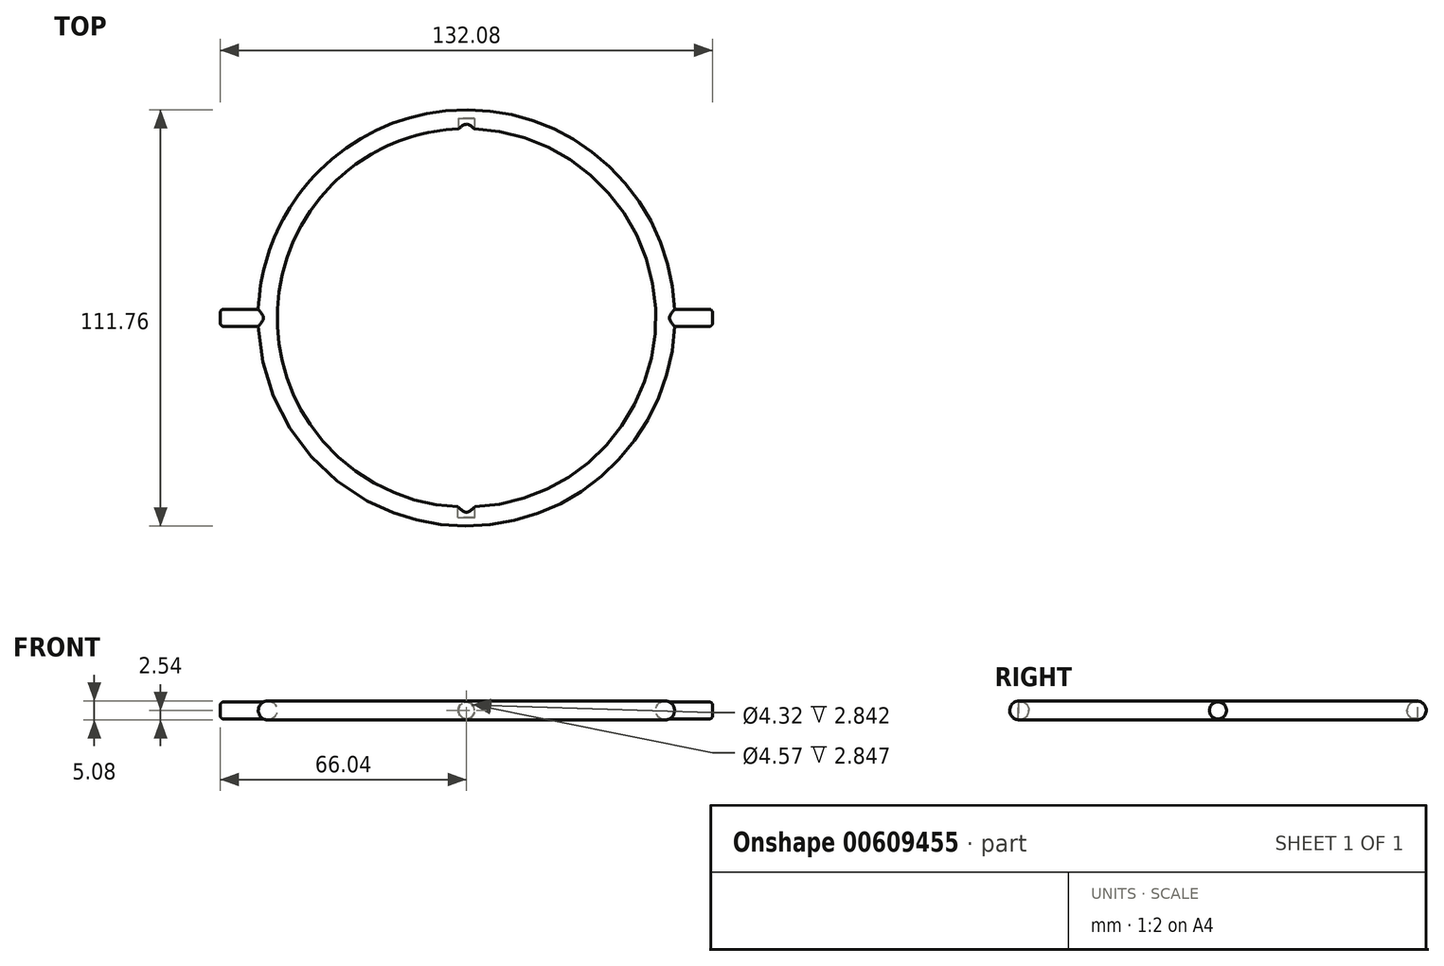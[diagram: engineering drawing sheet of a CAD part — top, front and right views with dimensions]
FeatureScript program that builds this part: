
annotation { "Feature Type Name" : "Feature", "Feature Type Description" : "" }
export const myFeature = defineFeature(function(context is Context, id is Id, definition is map)
    precondition{}
    {
        {
            var Q0;
            Q0=qCreatedBy(makeId("Top.planeOp"),FACE);
            var sketch = newSketch(context, id + "F0", { "sketchPlane" : qUnion([Q0])});
            skCircle(sketch, "E0", {"center": v(0, 0) * mm, "radius": 53.34 * mm});
            skSolve(sketch);
        }
        {
            var Q0;
            Q0=qCreatedBy(makeId("Right.planeOp"),FACE);
            var sketch = newSketch(context, id + "F1", { "sketchPlane" : qUnion([Q0])});
            skCircle(sketch, "E1", {"center": v(-53.34, 0) * mm, "radius": 2.54 * mm});
            skSolve(sketch);
        }
        {
            var Q0;
            Q0=makeQuery(id+"F1.imprint","IMPRINT",FACE,{"disambiguationData":[TD([[makeQuery(id+"F1.imprint","IMPRINT",EDGE,{"derivedFrom":sQuery(id+"F1.wireOp",EDGE,"E1")}),1.0]])]});
            var Q1;
            Q1=sQuery(id+"F0.wireOp",EDGE,"E0");
            sweep(context, id + "F2", {"profiles" : qUnion([Q0]), "path" : qUnion([Q1])});
        }
        {
            var Q0;
            Q0=qCreatedBy(makeId("Front.planeOp"),FACE);
            cPlane(context, id + "F3", {"entities" : qUnion([Q0]), "cplaneType" : CPlaneType.OFFSET, "offset" : 49.53 * mm, "oppositeDirection" : true, "width" : 152.4 * mm, "height" : 152.4 * mm});
        }
        {
            var Q0;
            Q0=qCreatedBy(id+"F3.planeOp",FACE);
            var sketch = newSketch(context, id + "F4", { "sketchPlane" : qUnion([Q0])});
            skCircle(sketch, "E2", {"center": v(0, 0) * mm, "radius": 2.16 * mm});
            skSolve(sketch);
        }
        {
            var Q0;
            Q0=makeQuery(id+"F4.imprint","IMPRINT",FACE,{"disambiguationData":[TD([[makeQuery(id+"F4.imprint","IMPRINT",EDGE,{"derivedFrom":sQuery(id+"F4.wireOp",EDGE,"E2")}),1.0]])]});
            var Q1;
            Q1=sQuery(id+"F4.wireOp",EDGE,"E2");
            extrude(context, id + "F5", {"entities" : qUnion([Q0]), "operationType" : NewBodyOperationType.REMOVE, "surfaceEntities" : qUnion([Q1]), "oppositeDirection" : true, "depth" : 4.06 * mm, "offsetDistance" : 25.4 * mm});
        }
        {
            var Q0;
            Q0=qCreatedBy(makeId("Front.planeOp"),FACE);
            cPlane(context, id + "F6", {"entities" : qUnion([Q0]), "cplaneType" : CPlaneType.OFFSET, "offset" : 49.53 * mm, "width" : 152.4 * mm, "height" : 152.4 * mm});
        }
        {
            var Q0;
            Q0=qCreatedBy(id+"F6.planeOp",FACE);
            var sketch = newSketch(context, id + "F7", { "sketchPlane" : qUnion([Q0])});
            skCircle(sketch, "E3", {"center": v(0, 0) * mm, "radius": 2.29 * mm});
            skSolve(sketch);
        }
        {
            var Q0;
            Q0=makeQuery(id+"F7.imprint","IMPRINT",FACE,{"disambiguationData":[TD([[makeQuery(id+"F7.imprint","IMPRINT",EDGE,{"derivedFrom":sQuery(id+"F7.wireOp",EDGE,"E3")}),1.0]])]});
            extrude(context, id + "F8", {"entities" : qUnion([Q0]), "operationType" : NewBodyOperationType.REMOVE, "depth" : 4.06 * mm, "offsetDistance" : 25.4 * mm});
        }
        {
            var Q0;
            Q0=qCreatedBy(makeId("Right.planeOp"),FACE);
            cPlane(context, id + "F9", {"entities" : qUnion([Q0]), "cplaneType" : CPlaneType.OFFSET, "offset" : 66.04 * mm, "width" : 152.4 * mm, "height" : 152.4 * mm});
        }
        {
            var Q0;
            Q0=qCreatedBy(id+"F9.planeOp",FACE);
            var sketch = newSketch(context, id + "F10", { "sketchPlane" : qUnion([Q0])});
            skCircle(sketch, "E4", {"center": v(0, 0) * mm, "radius": 2.29 * mm});
            skSolve(sketch);
        }
        {
            var Q0;
            Q0=makeQuery(id+"F10.imprint","IMPRINT",FACE,{"disambiguationData":[TD([[makeQuery(id+"F10.imprint","IMPRINT",EDGE,{"derivedFrom":sQuery(id+"F10.wireOp",EDGE,"E4")}),1.0]])]});
            extrude(context, id + "F11", {"entities" : qUnion([Q0]), "operationType" : NewBodyOperationType.ADD, "endBound" : BoundingType.UP_TO_NEXT, "oppositeDirection" : true, "depth" : 25.4 * mm, "offsetDistance" : 25.4 * mm});
        }
        {
            var Q0;
            Q0=makeQuery(id+"F11.opExtrude","CAP_EDGE",EDGE,{"disambiguationData":[OSD([sQuery(id+"F10.wireOp",EDGE,"E4")])],"isStart":true});
            fillet(context, id + "F12", {"entities" : qUnion([Q0]), "radius" : 0.89 * mm, "tangentPropagation" : true, "allowEdgeOverflow" : false});
        }
        {
            var Q0;
            Q0=makeQuery(id+"F2.opSweep","SWEPT_BODY",BODY,{"disambiguationData":[OSD([sQuery(id+"F0.wireOp",EDGE,"E0"),sQuery(id+"F1.wireOp",EDGE,"E1")])]});
            var Q1;
            Q1=qCreatedBy(makeId("Right.planeOp"),FACE);
            mirror(context, id + "F13", {"operationType" : NewBodyOperationType.ADD, "entities" : qUnion([Q0]), "mirrorPlane" : qUnion([Q1])});
        }
    });
